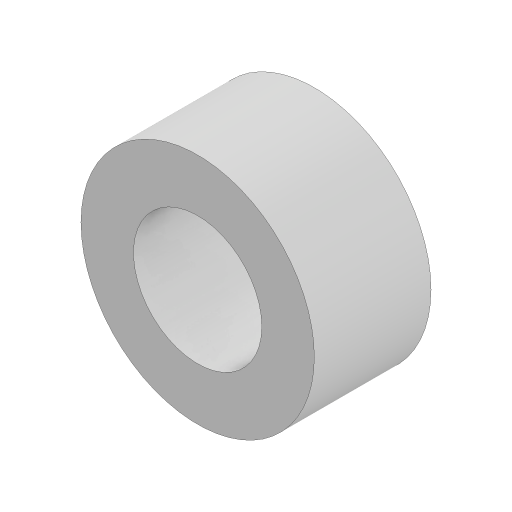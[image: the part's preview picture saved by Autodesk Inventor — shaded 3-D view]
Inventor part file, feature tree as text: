
AUTODESK INVENTOR PART (.ipt)
format: ipt  version: 2023 (Build 270158000, 158)  size: 101,888 bytes
history: native  units: mm
features: extrude x1, sketch x1
ambient origin geometry x8: Origin, YZ Plane, XZ Plane, XY Plane, X Axis, Y Axis, Z Axis, Center Point
bodies: Solid1 (feature_tree)
feature tree (2):
  extrude  "Extrusion1"  Depth=2.0mm
  sketch  "Sketch1"  dims[d0=2.2mm d1=4.0mm d2=2.0mm d3=0.0mm]
